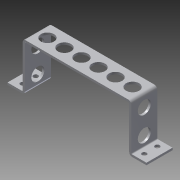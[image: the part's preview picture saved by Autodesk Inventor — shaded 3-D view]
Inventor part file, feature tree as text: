
AUTODESK INVENTOR PART (.ipt)
format: ipt  version: 2013 (Build 170138000, 138)  size: 209,920 bytes
history: native  units: in
note: dims shown in document units (in); Inventor stores cm internally (conversion verified against a paired STEP export)
features: sheet_metal_op x13, sketch x8, other x8
ambient origin geometry x8: Origin, YZ Plane, XZ Plane, XY Plane, X Axis, Y Axis, Z Axis, Center Point
bodies: Solid1 (feature_tree)
feature tree (29):
  sheet_metal_op  "Face1"
  sheet_metal_op  "Flange1"
  sheet_metal_op  "Flange2"
  sheet_metal_op  "Flange3"
  sheet_metal_op  "Flange4"
  sketch  "Sketch1"  dims[d0=1.5in]
  other  "Plate1"
  sketch  "Sketch2"  dims[d1=1.0in]
  other  "Plate2"
  sheet_metal_op  "Bend1"
  sheet_metal_op  "Corner1"
  sketch  "Sketch3"  dims[d2=0.266in]
  other  "Plate3"
  sheet_metal_op  "Bend2"
  sheet_metal_op  "Corner2"
  sketch  "Sketch4"  dims[d3=0.75in]
  other  "Plate4"
  sheet_metal_op  "Bend3"
  sheet_metal_op  "Corner3"
  sketch  "Sketch5"  dims[d4=0.375in]
  other  "Plate5"
  sheet_metal_op  "Bend4"
  sheet_metal_op  "Corner4"
  sketch  "Sketch6"  dims[d5=0.125in]
  sketch  "Sketch7"  dims[d6=0.125in]
  sketch  "Sketch8"  dims[d7=0.0625in d8=0.25in d9=0.125in d10=2.75in d11=90.0deg d12=0.05in d13=0.5in d14=0.125in d15=0.125in d16=0.125in d17=0.0625in d18=0.25in d19=0.125in d20=6.25in d21=90.0deg d22=0.05in d23=0.5in d24=0.125in d25=0.125in d26=0.125in d27=0.0625in d28=0.25in d29=0.125in d30=2.75in d31=90.0deg d32=0.05in d33=0.5in d34=0.125in d35=0.125in d36=0.125in d37=0.0625in d38=0.25in d39=0.125in d40=1.0in d41=90.0deg d42=0.05in d43=0.5in d44=0.125in d45=0.125in d46=0.5in d47=0.266in d48=0.75in d49=0.375in d50=0.125in d51=0.0in d52=5.9in d53=0.5in d54=2.3622in d56=0.98in d57=0.3937in d59=1.0in d61=0.75in d62=0.125in d63=0.0in d64=0.75in d66=0.5in d67=0.5in d68=200.0in d69=0.0in]
  other  "Cut1"
  other  "Cut2"
  other  "Cut3"
